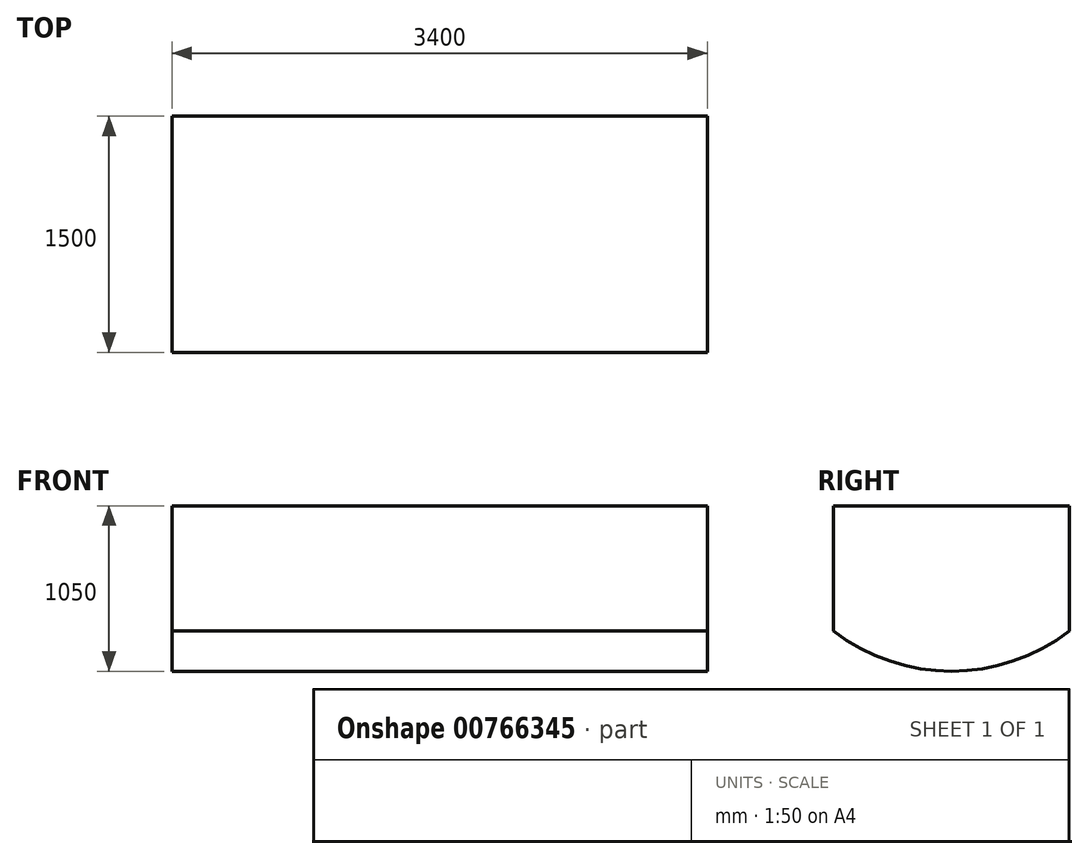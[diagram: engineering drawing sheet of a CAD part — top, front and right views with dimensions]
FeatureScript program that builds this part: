
annotation { "Feature Type Name" : "Feature", "Feature Type Description" : "" }
export const myFeature = defineFeature(function(context is Context, id is Id, definition is map)
    precondition{}
    {
        {
            var Q0;
            Q0=qCreatedBy(makeId("Right.planeOp"),FACE);
            var sketch = newSketch(context, id + "F0", { "sketchPlane" : qUnion([Q0])});
            skLineSegment(sketch, "E0", {"start": v(-597.62, 429.18) * mm, "end": v(902.38, 429.18) * mm});
            skLineSegment(sketch, "E1", {"start": v(-597.62, 429.18) * mm, "end": v(-597.62, -364.9) * mm});
            skLineSegment(sketch, "E2", {"start": v(902.38, 429.18) * mm, "end": v(902.38, -364.9) * mm});
            skArc(sketch, "E3", {"start": v(-597.62, -364.9) * mm, "mid": v(152.38, -620.82) * mm, "end": v(902.38, -364.9) * mm});
            skLineSegment(sketch, "E4", {"start": v(152.38, 429.18) * mm, "end": v(152.38, -620.82) * mm, "construction": true});
            skSolve(sketch);
        }
        {
            var Q0;
            Q0=makeQuery(id+"F0.imprint","IMPRINT",FACE,{"disambiguationData":[TD([[makeQuery(id+"F0.imprint","IMPRINT",EDGE,{"derivedFrom":sQuery(id+"F0.wireOp",EDGE,"E0")}),-1.0]])]});
            extrude(context, id + "F1", {"entities" : qUnion([Q0]), "endBound" : BoundingType.SYMMETRIC, "depth" : 3400 * mm, "offsetDistance" : 25 * mm});
        }
    });
